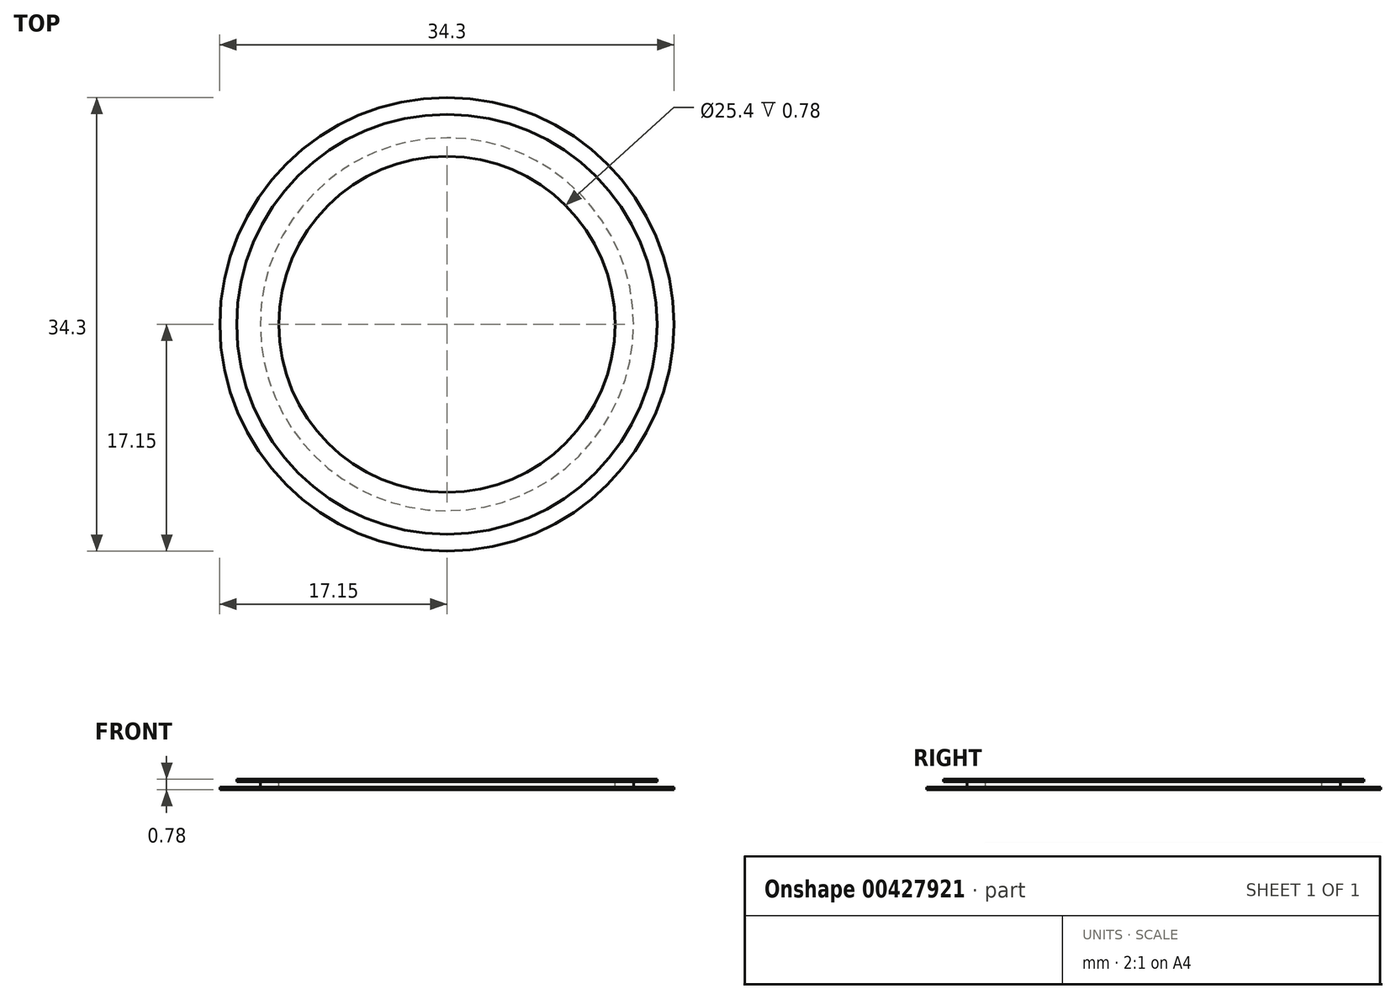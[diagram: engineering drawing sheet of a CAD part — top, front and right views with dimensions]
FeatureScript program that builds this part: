
annotation { "Feature Type Name" : "Feature", "Feature Type Description" : "" }
export const myFeature = defineFeature(function(context is Context, id is Id, definition is map)
    precondition{}
    {
        {
            assignVariable(context, id + "F0", {"name" : "M10_thk", "anyValue" : .19});
        }
        {
            assignVariable(context, id + "F1", {"name" : "shaper_relief", "anyValue" : .4});
        }
        {
            assignVariable(context, id + "F2", {"name" : "M11_thk", "anyValue" : .19});
        }
        {
            var Q0;
            Q0=qCreatedBy(makeId("Top.planeOp"),FACE);
            var sketch = newSketch(context, id + "F3", { "sketchPlane" : qUnion([Q0])});
            skCircle(sketch, "E0", {"center": v(0, 0) * mm, "radius": 15.88 * mm, "construction": true});
            skCircle(sketch, "E1", {"center": v(0, 0) * mm, "radius": 12.7 * mm});
            skCircle(sketch, "E2.0", {"center": v(0, 0) * mm, "radius": 17.14 * mm});
            skCircle(sketch, "E3.0", {"center": v(0, 0) * mm, "radius": 14.35 * mm, "construction": true});
            skSolve(sketch);
        }
        {
            var Q0;
            Q0=qSketchRegion(id+"F3",true);
            var Q1;
            Q1=makeQuery(id+"FxT4LMIPvkr7pVi_0.merge.F8IFZMx4UYxcvl3_3.opExtrude","CAP_FACE",FACE,{"disambiguationData":[OSD([sQuery(id+"FxT4LMIPvkr7pVi_0.merge.FnZUuLZ2Xg5gS1P_3.wireOp",EDGE,"72a3510d-0ac6-468e-a638-e444c5b63404.0")])],"isStart":true});
            extrude(context, id + "F4", {"entities" : qUnion([Q0]), "oppositeDirection" : true, "endBoundEntityFace" : qUnion([Q1]), "depth" : (getVariable(context, 'M10_thk')) * mm});
        }
        {
            var Q0;
            Q0=makeQuery(id+"F3.imprint","IMPRINT",FACE,{"disambiguationData":[TD([[makeQuery(id+"F3.imprint","IMPRINT",EDGE,{"derivedFrom":sQuery(id+"F3.wireOp",EDGE,"E1")}),-1.0]])]});
            var sketch = newSketch(context, id + "F5", { "sketchPlane" : qUnion([Q0])});
            skCircle(sketch, "E4.0", {"center": v(0, 0) * mm, "radius": 14.1 * mm});
            skCircle(sketch, "E5.0", {"center": v(0, 0) * mm, "radius": 12.7 * mm});
            skSolve(sketch);
        }
        {
            var Q0;
            Q0=qSketchRegion(id+"F5",true);
            extrude(context, id + "F6", {"entities" : qUnion([Q0]), "operationType" : NewBodyOperationType.ADD, "depth" : (getVariable(context, 'shaper_relief')) * mm});
        }
        {
            var Q0;
            Q0=makeQuery(id+"F6.opExtrude","CAP_FACE",FACE,{"disambiguationData":[OSD([sQuery(id+"F5.wireOp",EDGE,"E4.0"),sQuery(id+"F5.wireOp",EDGE,"E5.0")])],"isStart":false});
            var sketch = newSketch(context, id + "F7", { "sketchPlane" : qUnion([Q0])});
            skCircle(sketch, "E6.1", {"center": v(0, 0) * mm, "radius": 12.7 * mm});
            skCircle(sketch, "E7.0", {"center": v(0, 0) * mm, "radius": 15.88 * mm});
            skSolve(sketch);
        }
        {
            var Q0;
            Q0=qSketchRegion(id+"F7",true);
            var Q1;
            Q1=makeQuery(id+"F6.opExtrude","CAP_FACE",FACE,{"disambiguationData":[OSD([sQuery(id+"FxT4LMIPvkr7pVi_0.merge.FvlJmh4ROpZrq48_4.wireOp",EDGE,"8f15afeb-7a04-4261-af85-0c532aafef5c.0")])],"isStart":false});
            extrude(context, id + "F8", {"entities" : qUnion([Q0]), "operationType" : NewBodyOperationType.ADD, "endBoundEntityFace" : qUnion([Q1]), "depth" : (getVariable(context, 'M11_thk')) * mm});
        }
    });
